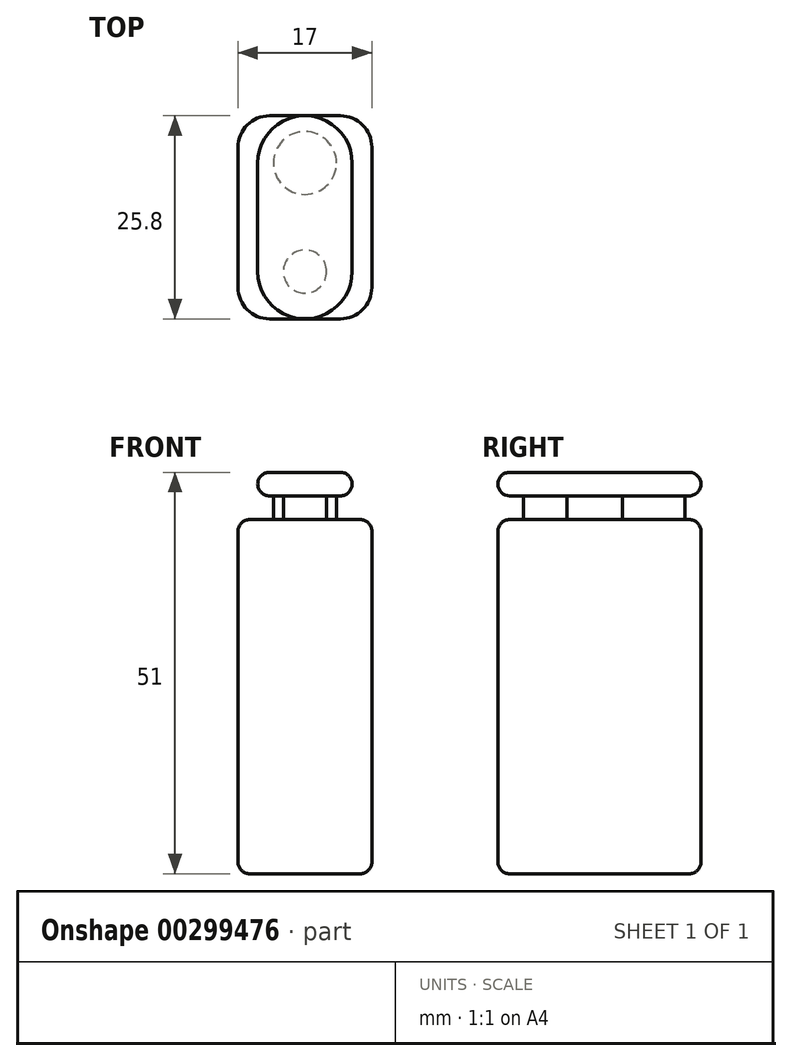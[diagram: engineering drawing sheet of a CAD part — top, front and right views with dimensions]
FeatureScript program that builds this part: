
annotation { "Feature Type Name" : "Feature", "Feature Type Description" : "" }
export const myFeature = defineFeature(function(context is Context, id is Id, definition is map)
    precondition{}
    {
        {
            var Q0;
            Q0=qCreatedBy(makeId("Top.planeOp"),FACE);
            var sketch = newSketch(context, id + "F0", { "sketchPlane" : qUnion([Q0])});
            skLineSegment(sketch, "E0.bottom", {"start": v(0, 0) * mm, "end": v(-17, 0) * mm});
            skLineSegment(sketch, "E0.top", {"start": v(0, 25.8) * mm, "end": v(-17, 25.8) * mm});
            skLineSegment(sketch, "E0.left", {"start": v(0, 0) * mm, "end": v(0, 25.8) * mm});
            skLineSegment(sketch, "E0.right", {"start": v(-17, 0) * mm, "end": v(-17, 25.8) * mm});
            skSolve(sketch);
        }
        {
            var Q0;
            Q0 = qSketchRegion(id + "F0", true);
            extrude(context, id + "F1", {"entities" : qUnion([Q0]), "depth" : 45 * mm});
        }
        {
            var Q0;
            Q0=makeQuery(id+"F1.opExtrude","SWEPT_EDGE",EDGE,{"disambiguationData":[OSD([sQuery(id+"F0.wireOp",EDGE,"E0.bottom"),sQuery(id+"F0.wireOp",EDGE,"E0.left")])]});
            var Q1;
            Q1=makeQuery(id+"F1.opExtrude","SWEPT_EDGE",EDGE,{"disambiguationData":[OSD([sQuery(id+"F0.wireOp",EDGE,"E0.top"),sQuery(id+"F0.wireOp",EDGE,"E0.left")])]});
            var Q2;
            Q2=makeQuery(id+"F1.opExtrude","SWEPT_EDGE",EDGE,{"disambiguationData":[OSD([sQuery(id+"F0.wireOp",EDGE,"E0.top"),sQuery(id+"F0.wireOp",EDGE,"E0.right")])]});
            var Q3;
            Q3=makeQuery(id+"F1.opExtrude","SWEPT_EDGE",EDGE,{"disambiguationData":[OSD([sQuery(id+"F0.wireOp",EDGE,"E0.bottom"),sQuery(id+"F0.wireOp",EDGE,"E0.right")])]});
            fillet(context, id + "F2", {"entities" : qUnion([Q0, Q1, Q2, Q3]), "radius" : 4 * mm, "tangentPropagation" : true, "allowEdgeOverflow" : false});
        }
        {
            var Q0;
            Q0=makeQuery(id+"F1.opExtrude","CAP_FACE",FACE,{"disambiguationData":[OSD([sQuery(id+"F0.wireOp",EDGE,"E0.bottom"),sQuery(id+"F0.wireOp",EDGE,"E0.top"),sQuery(id+"F0.wireOp",EDGE,"E0.left"),sQuery(id+"F0.wireOp",EDGE,"E0.right")])],"isStart":false});
            var Q1;
            Q1=makeQuery(id+"F1.opExtrude","CAP_FACE",FACE,{"disambiguationData":[OSD([sQuery(id+"F0.wireOp",EDGE,"E0.bottom"),sQuery(id+"F0.wireOp",EDGE,"E0.top"),sQuery(id+"F0.wireOp",EDGE,"E0.left"),sQuery(id+"F0.wireOp",EDGE,"E0.right")])],"isStart":true});
            fillet(context, id + "F3", {"entities" : qUnion([Q0, Q1]), "radius" : 1.5 * mm, "tangentPropagation" : true, "allowEdgeOverflow" : false});
        }
        {
            var Q0;
            Q0=makeQuery(id+"F1.opExtrude","CAP_FACE",FACE,{"disambiguationData":[OSD([sQuery(id+"F0.wireOp",EDGE,"E0.bottom"),sQuery(id+"F0.wireOp",EDGE,"E0.top"),sQuery(id+"F0.wireOp",EDGE,"E0.left"),sQuery(id+"F0.wireOp",EDGE,"E0.right")])],"isStart":false});
            var sketch = newSketch(context, id + "F4", { "sketchPlane" : qUnion([Q0])});
            skCircle(sketch, "E1", {"center": v(-8.5, 19.8) * mm, "radius": 4 * mm});
            skCircle(sketch, "E2", {"center": v(-8.5, 6) * mm, "radius": 2.75 * mm});
            skLineSegment(sketch, "E3", {"start": v(-8.5, 24.3) * mm, "end": v(-8.5, 1.5) * mm, "construction": true});
            skSolve(sketch);
        }
        {
            var Q0;
            Q0 = qSketchRegion(id + "F4", true);
            extrude(context, id + "F5", {"entities" : qUnion([Q0]), "operationType" : NewBodyOperationType.ADD, "depth" : 3 * mm});
        }
        {
            var Q0;
            Q0=makeQuery(id+"F5.opExtrude","CAP_FACE",FACE,{"disambiguationData":[OSD([sQuery(id+"F4.wireOp",EDGE,"E1")])],"isStart":false});
            var sketch = newSketch(context, id + "F6", { "sketchPlane" : qUnion([Q0])});
            skArc(sketch, "E4", {"start": v(-2.5, 19.8) * mm, "mid": v(-8.5, 25.8) * mm, "end": v(-14.5, 19.8) * mm});
            skArc(sketch, "E5", {"start": v(-14.5, 6) * mm, "mid": v(-8.5, 0) * mm, "end": v(-2.5, 6) * mm});
            skLineSegment(sketch, "E6", {"start": v(-2.5, 19.8) * mm, "end": v(-2.5, 6) * mm});
            skLineSegment(sketch, "E7", {"start": v(-14.5, 19.8) * mm, "end": v(-14.5, 6) * mm});
            skSolve(sketch);
        }
        {
            var Q0;
            Q0 = qSketchRegion(id + "F6", true);
            extrude(context, id + "F7", {"entities" : qUnion([Q0]), "operationType" : NewBodyOperationType.ADD, "depth" : 3 * mm});
        }
        {
            var Q0;
            Q0=makeQuery(id+"F7.opExtrude","CAP_FACE",FACE,{"disambiguationData":[OSD([sQuery(id+"F6.wireOp",EDGE,"E4"),sQuery(id+"F6.wireOp",EDGE,"E5"),sQuery(id+"F6.wireOp",EDGE,"E6"),sQuery(id+"F6.wireOp",EDGE,"E7")])],"isStart":false});
            var Q1;
            Q1=makeQuery(id+"F7.opExtrude","CAP_EDGE",EDGE,{"disambiguationData":[OSD([sQuery(id+"F6.wireOp",EDGE,"E7")])],"isStart":true});
            fillet(context, id + "F8", {"entities" : qUnion([Q0, Q1]), "radius" : 1.5 * mm, "tangentPropagation" : true, "allowEdgeOverflow" : false});
        }
    });
